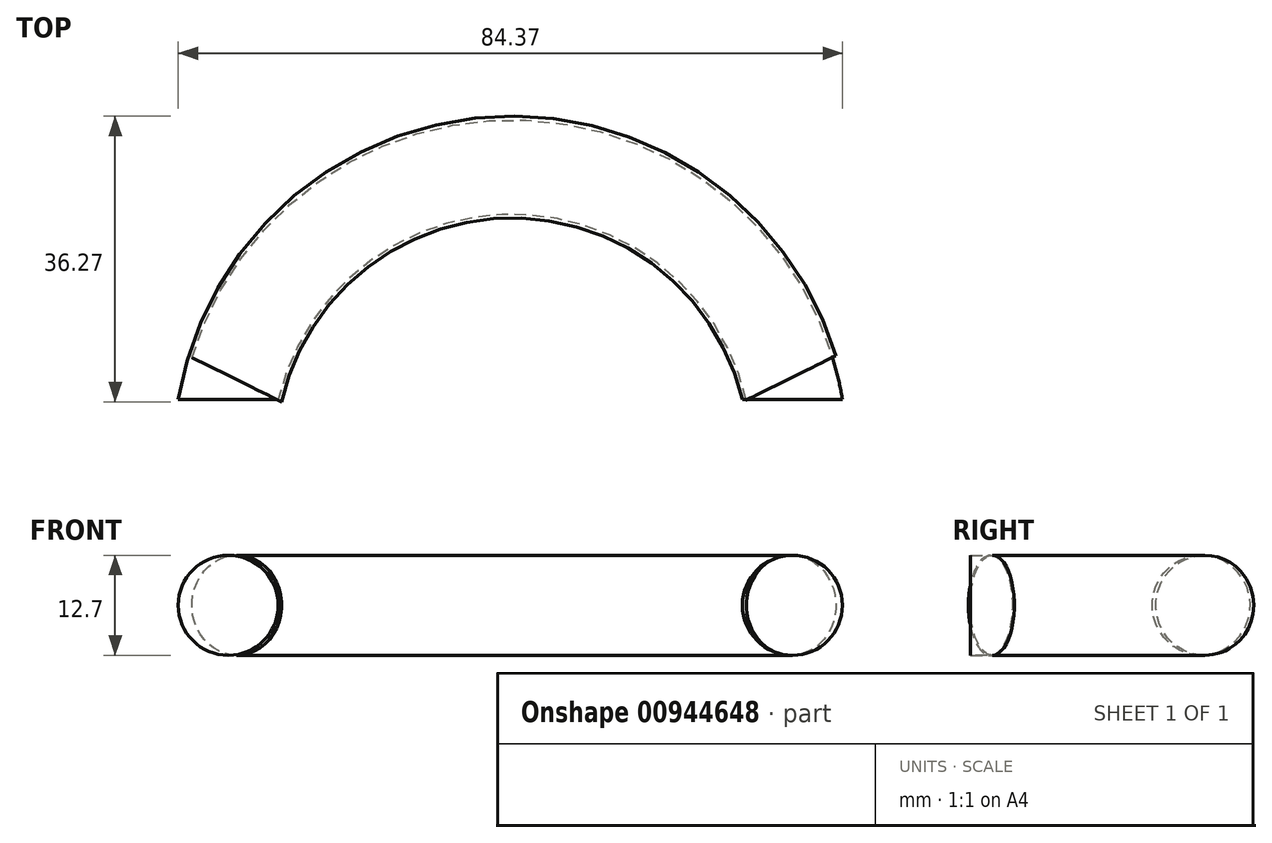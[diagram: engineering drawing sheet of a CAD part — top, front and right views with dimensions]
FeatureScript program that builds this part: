
annotation { "Feature Type Name" : "Feature", "Feature Type Description" : "" }
export const myFeature = defineFeature(function(context is Context, id is Id, definition is map)
    precondition{}
    {
        {
            var Q0;
            Q0=qCreatedBy(makeId("Front.planeOp"),FACE);
            var sketch = newSketch(context, id + "F0", { "sketchPlane" : qUnion([Q0])});
            skCircle(sketch, "E0", {"center": v(-34.37, 0) * mm, "radius": 6.35 * mm});
            skCircle(sketch, "E1", {"center": v(37.3, 0) * mm, "radius": 6.35 * mm});
            skSolve(sketch);
        }
        {
            var Q0;
            Q0=qCreatedBy(makeId("Top.planeOp"),FACE);
            var sketch = newSketch(context, id + "F1", { "sketchPlane" : qUnion([Q0])});
            skArc(sketch, "E2", {"start": v(31.56, 0) * mm, "mid": v(1.7, 23.67) * mm, "end": v(-28.15, 0) * mm});
            skArc(sketch, "E3", {"start": v(44.65, 0) * mm, "mid": v(2.1, 34.78) * mm, "end": v(-40.46, 0) * mm});
            skLineSegment(sketch, "E4", {"start": v(-40.46, 0) * mm, "end": v(-28.15, 0) * mm});
            skLineSegment(sketch, "E5", {"start": v(31.56, 0) * mm, "end": v(44.65, 0) * mm});
            skSolve(sketch);
        }
        {
            var Q0;
            Q0=makeQuery(id+"F0.imprint","IMPRINT",FACE,{"disambiguationData":[TD([[makeQuery(id+"F0.imprint","IMPRINT",EDGE,{"derivedFrom":sQuery(id+"F0.wireOp",EDGE,"E0")}),1.0]])]});
            var Q1;
            Q1=makeQuery(id+"F0.imprint","IMPRINT",FACE,{"disambiguationData":[TD([[makeQuery(id+"F0.imprint","IMPRINT",EDGE,{"derivedFrom":sQuery(id+"F0.wireOp",EDGE,"E1")}),1.0]])]});
            var Q2;
            Q2=sQuery(id+"F1.wireOp",EDGE,"E2");
            sweep(context, id + "F2", {"profiles" : qUnion([Q0, Q1]), "path" : qUnion([Q2])});
        }
    });
